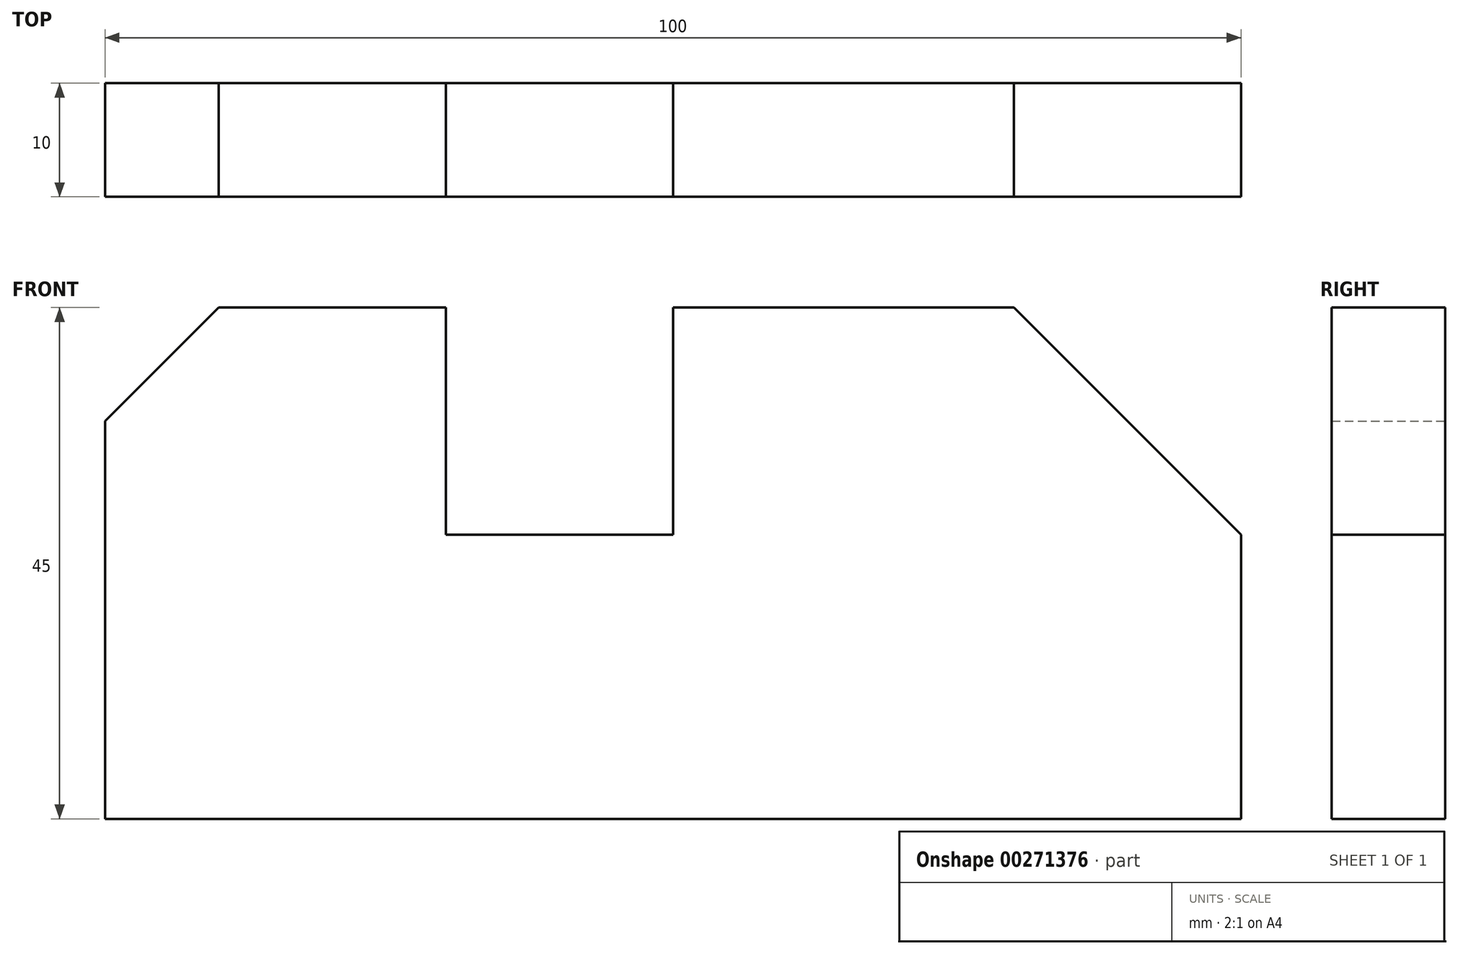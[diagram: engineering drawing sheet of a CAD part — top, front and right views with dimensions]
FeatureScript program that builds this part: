
annotation { "Feature Type Name" : "Feature", "Feature Type Description" : "" }
export const myFeature = defineFeature(function(context is Context, id is Id, definition is map)
    precondition{}
    {
        {
            var Q0;
            Q0=qCreatedBy(makeId("Front.planeOp"),FACE);
            var sketch = newSketch(context, id + "F0", { "sketchPlane" : qUnion([Q0])});
            skLineSegment(sketch, "E0", {"start": v(0, 0) * mm, "end": v(100, 0) * mm});
            skLineSegment(sketch, "E1", {"start": v(0, 0) * mm, "end": v(0, 35) * mm});
            skLineSegment(sketch, "E2", {"start": v(0, 35) * mm, "end": v(10, 45) * mm});
            skLineSegment(sketch, "E3", {"start": v(10, 45) * mm, "end": v(30, 45) * mm});
            skLineSegment(sketch, "E4", {"start": v(30, 45) * mm, "end": v(30, 25) * mm});
            skLineSegment(sketch, "E5", {"start": v(30, 25) * mm, "end": v(50, 25) * mm});
            skLineSegment(sketch, "E6", {"start": v(50, 25) * mm, "end": v(50, 45) * mm});
            skLineSegment(sketch, "E7", {"start": v(100, 0) * mm, "end": v(100, 25) * mm});
            skLineSegment(sketch, "E8", {"start": v(100, 25) * mm, "end": v(80, 45) * mm});
            skLineSegment(sketch, "E9", {"start": v(50, 45) * mm, "end": v(80, 45) * mm});
            skSolve(sketch);
        }
        {
            var Q0;
            Q0=makeQuery(id+"F0.imprint","IMPRINT",FACE,{"disambiguationData":[TD([[makeQuery(id+"F0.imprint","IMPRINT",EDGE,{"derivedFrom":sQuery(id+"F0.wireOp",EDGE,"E0")}),1.0]])]});
            extrude(context, id + "F1", {"entities" : qUnion([Q0]), "depth" : 10 * mm});
        }
    });
